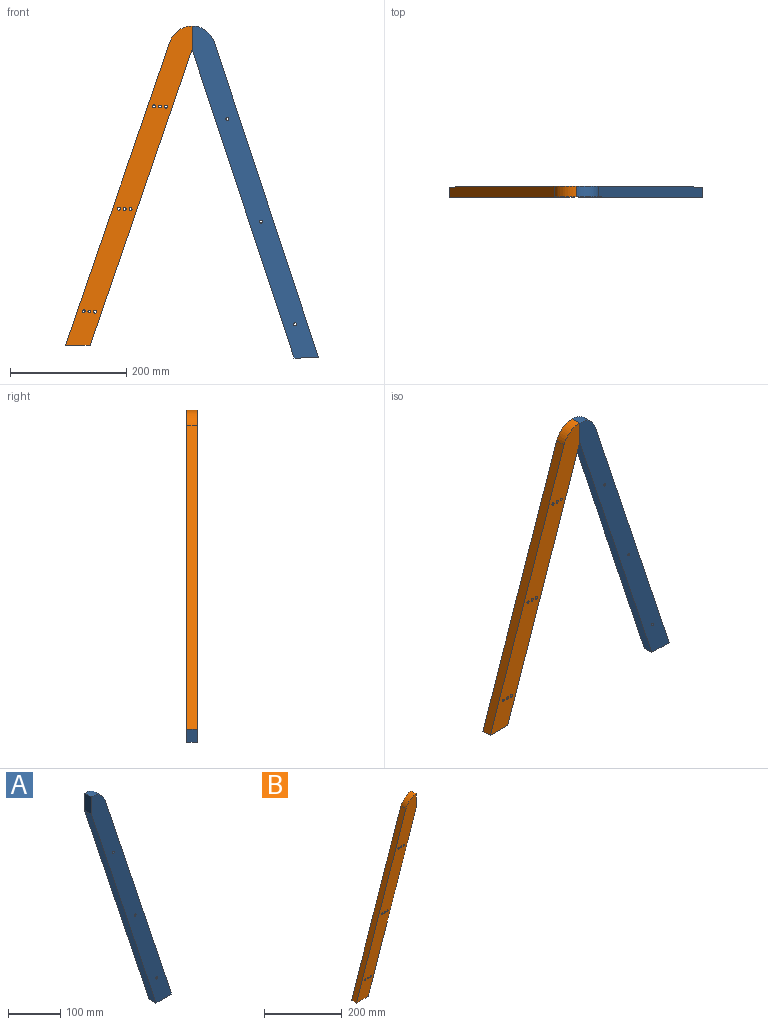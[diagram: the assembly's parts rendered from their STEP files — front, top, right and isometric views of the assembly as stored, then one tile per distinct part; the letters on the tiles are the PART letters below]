
ASSEMBLY  parts=2 mates=1
PART A: 10 faces, bbox 217.1x18x570 mm
  f0: cylinder r=40mm len=37.98mm, axis (0,1,0), area 901.4mm2, adj f1,f6,f8,f9
  f1: plane 40x18mm, normal (-1,0,0), area 720mm2, adj f0,f2,f8,f9
  f2: plane 530x175mm, normal (-0.95,0,-0.31), area 10046.6mm2, adj f1,f3,f8,f9
  f3: plane 42.12x18mm, normal (0,0,-1), area 758.2mm2, adj f2,f6,f8,f9
  f4: cylinder r=2.5mm len=18mm, axis (0,1,0), area 282.7mm2, adj f8,f9
  f5: cylinder r=2.5mm len=18mm, axis (0,1,0), area 282.7mm2, adj f8,f9
  f6: plane 542.54x179.14mm, normal (0.95,0,0.31), area 10284.3mm2, adj f0,f3,f8,f9
  f7: cylinder r=2.5mm len=18mm, axis (0,1,0), area 282.7mm2, adj f8,f9
  f8: plane 570x217.12mm, normal (0,-1,0), area 23532.5mm2, adj f0,f1,f2,f3,f4,f5,f6,f7
  f9: plane 570x217.12mm, normal (0,1,0), area 23532.5mm2, adj f0,f1,f2,f3,f4,f5,f6,f7
PART B: 20 faces, bbox 217.3x18x548.2 mm
  f0: plane 42.31x18mm, normal (0,0,-1), area 761.5mm2, adj f1,f12,f14,f15
  f1: plane 508.24x175mm, normal (0.95,0,-0.33), area 9675.4mm2, adj f0,f2,f14,f15
  f2: plane 40x18mm, normal (1,0,0), area 680.7mm2, adj f1,f3,f14,f15,f16,f18
  f3: cylinder r=40mm len=37.82mm, axis (0,1,0), area 892.2mm2, adj f2,f12,f14,f15
  f4: cylinder r=2.5mm len=18mm, axis (0,1,0), area 282.7mm2, adj f14,f15
  f5: cylinder r=2.5mm len=18mm, axis (0,1,0), area 282.7mm2, adj f14,f15
  f6: cylinder r=2.5mm len=18mm, axis (0,1,0), area 282.7mm2, adj f14,f15
  f7: cylinder r=2.5mm len=18mm, axis (0,1,0), area 282.7mm2, adj f14,f15
  f8: cylinder r=2.5mm len=18mm, axis (0,1,0), area 282.7mm2, adj f14,f15
  f9: cylinder r=2.5mm len=18mm, axis (0,1,0), area 282.7mm2, adj f14,f15
  f10: cylinder r=2.5mm len=18mm, axis (0,1,0), area 282.7mm2, adj f14,f15
  f11: cylinder r=2.5mm len=18mm, axis (0,1,0), area 282.7mm2, adj f14,f15
  f12: plane 521.26x179.48mm, normal (-0.95,0,0.33), area 9923.3mm2, adj f0,f3,f14,f15
  f13: cylinder r=2.5mm len=18mm, axis (0,1,0), area 282.7mm2, adj f14,f15
  f14: plane 548.24x217.31mm, normal (0,-1,0), area 22591mm2, adj f0,f1,f2,f3,f4,f5,f6,f7
  f15: plane 548.24x217.31mm, normal (0,1,0), area 22591mm2, adj f0,f1,f2,f3,f4,f5,f6,f7
  f16: cylinder r=2.5mm len=15mm, axis (1,0,0), area 235.6mm2, adj f2,f17
  f17: plane 5x5mm, normal (1,0,0), area 19.6mm2, adj f16
  f18: cylinder r=2.5mm len=15mm, axis (1,0,0), area 235.6mm2, adj f2,f19
  f19: plane 5x5mm, normal (1,0,0), area 19.6mm2, adj f18
PLACE A rot(axis=(0,-1,0),0deg) t=(-70.75,104.57,-31.01)mm
PLACE B rot(axis=(0.97,0.23,0.08),0deg) t=(-70.75,104.57,-9.25)mm
MATE revolute B.f3 <-> A.f0  axis (0,1,0) through (-70.75,95.57,498.99)mm
